# Revit family: Differential Pressure Control Valve 4007 5-30kPa
name_source: partatom
category: Rohrzubehör
revit_build: Autodesk Revit 2018 (Build: 20190510_1515(x64)
units: mm (PartAtom-declared; Revit-internal decimal feet)

## family parameters
Arbeitsebenenbasiert = Nein
Beim Laden mit Abzugskörper schneiden = Nein
Bemaßung runder Anschluss = Durchmesser verwenden
Gemeinsam genutzt = Nein
Immer vertikal = Ja
OmniClass-Nummer = 23.65.55.14.24
OmniClass-Titel = Mixing Valves for Liquid Services
Teiletyp = Unterbricht

## types (1)
- Differential Pressure Control Valve 4007 5-30kPa
    Application = For heating and cooling systems, to ensure constant differential pressure constant within the
control range.
Reset from HERZ STROMAX circuit regulating valves.
    Hersteller = HERZ-Armaturen Ges.m.b.H
    Materials = Ammonia contained in hemp can damage brass valve bodies, EPDM gaskets can be affected by
mineral oil lubricants and thus lead to failure of the EPDM seals. Please refer to manufacturers
documentation when using ethylene glycol products for frost and corrosion protection.
    Max. differential pressure on the body = 200000.0 Pa
    Max. operating pressure = 1600000.0 Pa
    Max. operating temperature DN15-DN32 = 130 °C
    Max. operating temperature DN40-DN80 = 110 °C
    Medium = Ethylene and propylene glycol is to be used in a mixing ratio of 25 - 50 Vol. [%].
Water quality according to ONORM H 5195 and VDI 2035
    Membrane and O-Rings = EPDM
    Min. operating temperature (frost protection) = -10 °C
    Min. operating temperature (frost protection, brass body) = -20 °C
    Min. operating temperature (pure water) = 2 °C
    Model = The differential pressure controller is a straight-version proportional controller and works without
auxiliary energy. The required nominal differential pressure can be continuously adjusted from 50 to
300 mbar. The adjusted set point can be read, locked and sealed. The nominal set point is factory
preset at minimum. The required set point is adjusted by means of a hand wheel and secured against
turning by the block ring. The impulse line (1000 mm) is included with the valve and is connected to a
circuit regulating valve in the supply line.
It is possible to connect HERZ STROMAX valves 4215, 4217 or 4218 AGF to a differential pressure
controller.
    SCRNCODE = 05;03;4
    SCRNSEQ = ARM;ARM_TYP="DIFR";2
    Set point spring = stainless steel
    Test pressure = 2400000.0 Pa
    URL = www.herzvalves.com
    Valve body = dezincification-resistant brass
    a1 = 9.5 mm  [stored 0.031168 ft]
    a2 = 21.02 mm
    a3 = 9.5 mm  [stored 0.031168 ft]
    h1 = 20.59 mm  [stored 0.0675525 ft]
    k1 = 21 mm  [stored 0.0688976 ft]
    k10 = 20.56 mm  [stored 0.0674541 ft]
    k11 = 45 mm  [stored 0.147638 ft]
    k12 = 39.28 mm
    k13 = 14 mm  [stored 0.0459318 ft]
    k14 = 101.66 mm  [stored 0.33353 ft]
    k16 = 7.28 mm  [stored 0.0238845 ft]
    k18 = 24.47 mm  [stored 0.0802822 ft]
    k19 = 24.47 mm  [stored 0.0802822 ft]
    k2 = 49.08 mm  [stored 0.161024 ft]
    k20 = 70.56 mm  [stored 0.231496 ft]
    k21 = 28.72 mm  [stored 0.0942257 ft]
    k22 = 3.22 mm  [stored 0.0105643 ft]
    k3 = 63 mm  [stored 0.206693 ft]
    k4 = 142.00°
    k5 = 11.83 mm  [stored 0.0388123 ft]
    k6 = 8.68 mm
    k7 = 9.45 mm  [stored 0.0310039 ft]
    k8 = 130.00°
    k9 = 17.65 mm  [stored 0.0579068 ft]
    m1 = 3.5 mm  [stored 0.0114829 ft]
    m3 = 4 mm  [stored 0.0131234 ft]
    t1 = 24.47 mm  [stored 0.0802822 ft]

note: [stored X ft] marks values corroborated as IEEE doubles in the binary element streams (Revit-internal decimal feet)
